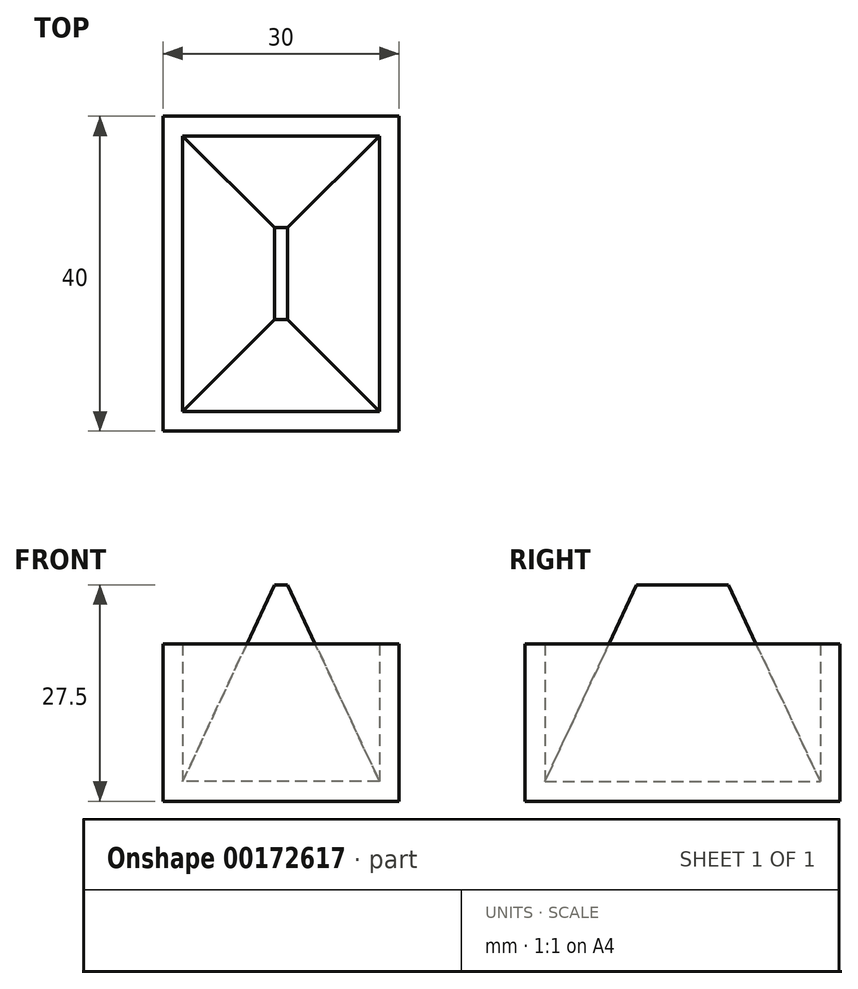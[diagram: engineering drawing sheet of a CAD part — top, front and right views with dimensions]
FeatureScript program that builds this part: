
annotation { "Feature Type Name" : "Feature", "Feature Type Description" : "" }
export const myFeature = defineFeature(function(context is Context, id is Id, definition is map)
    precondition{}
    {
        {
            var Q0;
            Q0=qCreatedBy(makeId("Top.planeOp"),FACE);
            var sketch = newSketch(context, id + "F0", { "sketchPlane" : qUnion([Q0])});
            skLineSegment(sketch, "E0.bottom", {"start": v(15, -20) * mm, "end": v(-15, -20) * mm});
            skLineSegment(sketch, "E0.top", {"start": v(15, 20) * mm, "end": v(-15, 20) * mm});
            skLineSegment(sketch, "E0.left", {"start": v(15, -20) * mm, "end": v(15, 20) * mm});
            skLineSegment(sketch, "E0.right", {"start": v(-15, -20) * mm, "end": v(-15, 20) * mm});
            skPoint(sketch, "E0.middle", {"position": v(0, 0) * mm});
            skSolve(sketch);
        }
        {
            var Q0;
            Q0=makeQuery(id+"F0.imprint","IMPRINT",FACE,{"disambiguationData":[TD([[makeQuery(id+"F0.imprint","IMPRINT",EDGE,{"derivedFrom":sQuery(id+"F0.wireOp",EDGE,"E0.bottom")}),-1.0]])]});
            extrude(context, id + "F1", {"entities" : qUnion([Q0]), "depth" : 20 * mm});
        }
        {
            var Q0;
            Q0=makeQuery(id+"F1.opExtrude","CAP_FACE",FACE,{"disambiguationData":[OSD([sQuery(id+"F0.wireOp",EDGE,"E0.bottom"),sQuery(id+"F0.wireOp",EDGE,"E0.top"),sQuery(id+"F0.wireOp",EDGE,"E0.left"),sQuery(id+"F0.wireOp",EDGE,"E0.right")])],"isStart":false});
            shell(context, id + "F2", {"entities" : qUnion([Q0]), "thickness" : 2.5 * mm});
        }
        {
            var Q0;
            Q0=makeQuery(id+"F2.opShell","OFFSET_FACE",FACE,{"disambiguationData":[OSD([sQuery(id+"F0.wireOp",EDGE,"E0.bottom"),sQuery(id+"F0.wireOp",EDGE,"E0.top"),sQuery(id+"F0.wireOp",EDGE,"E0.left"),sQuery(id+"F0.wireOp",EDGE,"E0.right")])]});
            var sketch = newSketch(context, id + "F3", { "sketchPlane" : qUnion([Q0])});
            skSolve(sketch);
        }
        {
            var Q0;
            {var subQ0=sQuery(id+"F0.wireOp",EDGE,"E0.bottom");Q0=makeQuery(id+"F3.imprint","IMPRINT",FACE,{"disambiguationData":[TD([[makeQuery(id+"F3.imprint","IMPRINT",EDGE,{"derivedFrom":makeQuery(id+"F2.opShell","OFFSET_EDGE",EDGE,{"disambiguationData":[OSD([subQ0]),TDD([makeQuery(id+"F1.opExtrude","CAP_EDGE",EDGE,{"disambiguationData":[OSD([subQ0])],"isStart":true})])]})}),-1.0]])]});}
            extrude(context, id + "F4", {"entities" : qUnion([Q0]), "operationType" : NewBodyOperationType.ADD, "depth" : 25 * mm, "hasDraft" : true, "draftAngle" : 25 * degree, "draftPullDirection" : true});
        }
    });
